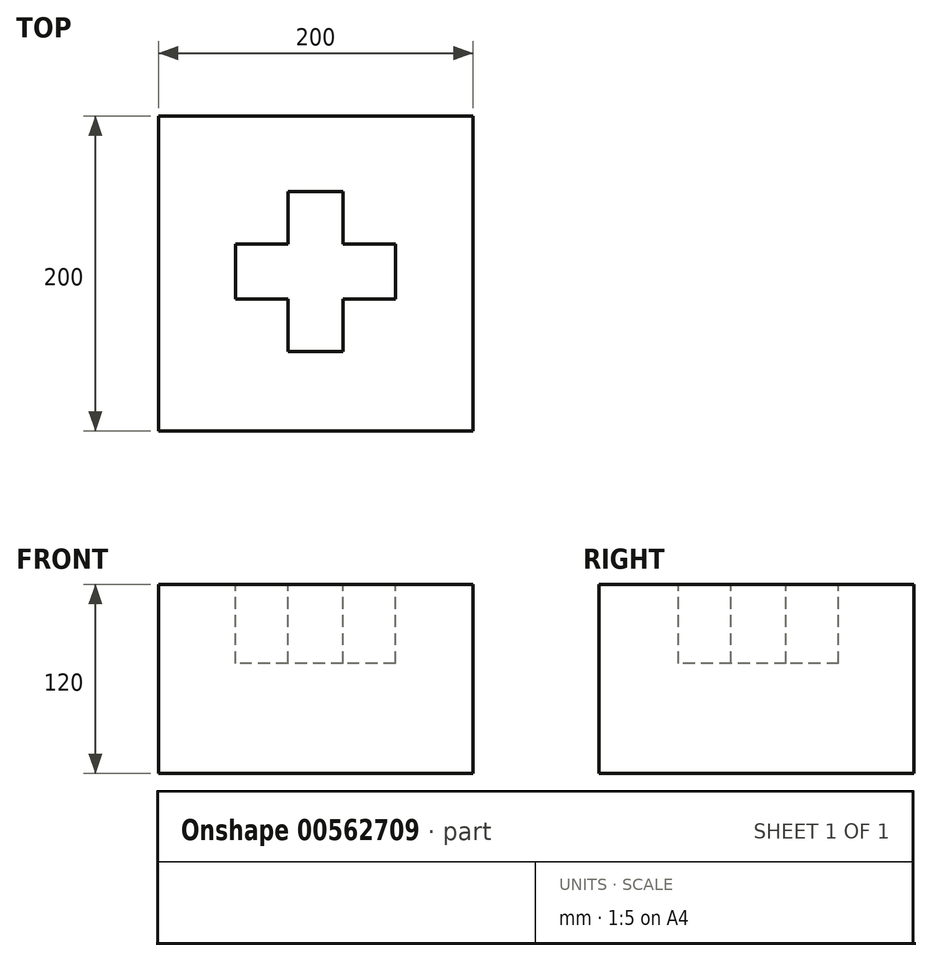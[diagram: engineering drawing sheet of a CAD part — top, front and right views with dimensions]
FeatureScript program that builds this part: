
annotation { "Feature Type Name" : "Feature", "Feature Type Description" : "" }
export const myFeature = defineFeature(function(context is Context, id is Id, definition is map)
    precondition{}
    {
        {
            var Q0;
            Q0=qCreatedBy(makeId("Top.planeOp"),FACE);
            var sketch = newSketch(context, id + "F0", { "sketchPlane" : qUnion([Q0])});
            skLineSegment(sketch, "E0.bottom", {"start": v(100.18, -101.26) * mm, "end": v(-99.82, -101.26) * mm});
            skLineSegment(sketch, "E0.top", {"start": v(100.18, 98.74) * mm, "end": v(-99.82, 98.74) * mm});
            skLineSegment(sketch, "E0.left", {"start": v(100.18, -101.26) * mm, "end": v(100.18, 98.74) * mm});
            skLineSegment(sketch, "E0.right", {"start": v(-99.82, -101.26) * mm, "end": v(-99.82, 98.74) * mm});
            skPoint(sketch, "E0.middle", {"position": v(0.18, -1.26) * mm});
            skSolve(sketch);
        }
        {
            var Q0;
            Q0 = qSketchRegion(id + "F0", true);
            extrude(context, id + "F1", {"entities" : qUnion([Q0]), "depth" : 120 * mm, "offsetDistance" : 25.4 * mm});
        }
        {
            var Q0;
            Q0=makeQuery(id+"F1.opExtrude","CAP_FACE",FACE,{"disambiguationData":[OSD([sQuery(id+"F0.wireOp",EDGE,"E0.bottom"),sQuery(id+"F0.wireOp",EDGE,"E0.top"),sQuery(id+"F0.wireOp",EDGE,"E0.left"),sQuery(id+"F0.wireOp",EDGE,"E0.right")])],"isStart":false});
            var sketch = newSketch(context, id + "F2", { "sketchPlane" : qUnion([Q0])});
            skLineSegment(sketch, "E1.bottom", {"start": v(17.5, 50.8) * mm, "end": v(-17.5, 50.8) * mm});
            skLineSegment(sketch, "E1.top", {"start": v(17.5, -50.8) * mm, "end": v(-17.5, -50.8) * mm});
            skLineSegment(sketch, "E1.left", {"start": v(17.5, 50.8) * mm, "end": v(17.5, -50.8) * mm});
            skLineSegment(sketch, "E1.right", {"start": v(-17.5, 50.8) * mm, "end": v(-17.5, -50.8) * mm});
            skPoint(sketch, "E1.middle", {"position": v(0, 0) * mm});
            skLineSegment(sketch, "E2.bottom", {"start": v(50.8, 17.5) * mm, "end": v(-50.8, 17.5) * mm});
            skLineSegment(sketch, "E2.top", {"start": v(50.8, -17.5) * mm, "end": v(-50.8, -17.5) * mm});
            skLineSegment(sketch, "E2.left", {"start": v(50.8, 17.5) * mm, "end": v(50.8, -17.5) * mm});
            skLineSegment(sketch, "E2.right", {"start": v(-50.8, 17.5) * mm, "end": v(-50.8, -17.5) * mm});
            skSolve(sketch);
        }
        {
            var Q0;
            Q0 = qSketchRegion(id + "F2", true);
            extrude(context, id + "F3", {"entities" : qUnion([Q0]), "operationType" : NewBodyOperationType.REMOVE, "oppositeDirection" : true, "depth" : 50 * mm, "offsetDistance" : 25.4 * mm});
        }
    });
